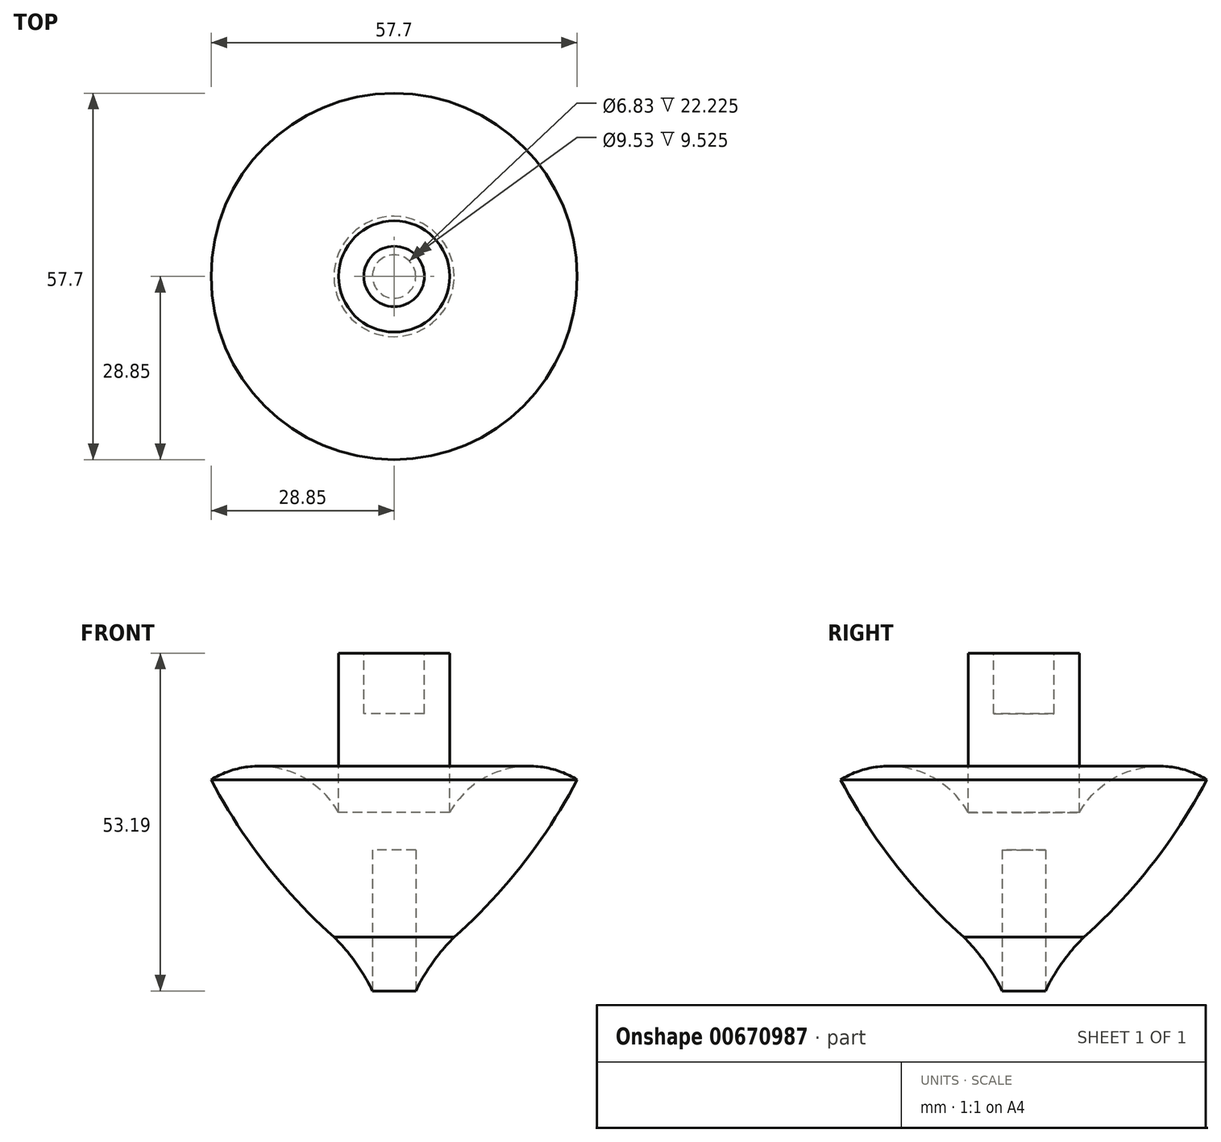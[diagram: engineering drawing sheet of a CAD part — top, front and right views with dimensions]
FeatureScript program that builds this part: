
annotation { "Feature Type Name" : "Feature", "Feature Type Description" : "" }
export const myFeature = defineFeature(function(context is Context, id is Id, definition is map)
    precondition{}
    {
        {
            var Q0;
            Q0=qCreatedBy(makeId("Front.planeOp"),FACE);
            var sketch = newSketch(context, id + "F0", { "sketchPlane" : qUnion([Q0])});
            skArc(sketch, "E0", {"start": v(9.48, 8.46) * mm, "mid": v(20.28, 20) * mm, "end": v(28.85, 33.28) * mm});
            skArc(sketch, "E1", {"start": v(28.85, 33.28) * mm, "mid": v(17.71, 34.95) * mm, "end": v(8.76, 28.11) * mm});
            skLineSegment(sketch, "E2", {"start": v(8.76, 28.11) * mm, "end": v(8.76, 53.19) * mm});
            skLineSegment(sketch, "E3", {"start": v(8.76, 53.19) * mm, "end": v(0, 53.19) * mm});
            skLineSegment(sketch, "E4", {"start": v(0, 53.19) * mm, "end": v(0, 0) * mm});
            skLineSegment(sketch, "E5", {"start": v(0, 0) * mm, "end": v(3.41, 0) * mm});
            skArc(sketch, "E6", {"start": v(9.48, 8.46) * mm, "mid": v(6.08, 4.5) * mm, "end": v(3.41, 0) * mm});
            skSolve(sketch);
        }
        {
            var Q0;
            Q0 = qSketchRegion(id + "F0", true);
            var Q1;
            Q1=sQuery(id+"F0.wireOp",EDGE,"E4");
            revolve(context, id + "F1", {"entities" : qUnion([Q0]), "axis" : qUnion([Q1]), "revolveType" : RevolveType.FULL, "surfaceOperationType" : NewSurfaceOperationType.NEW});
        }
        {
            var Q0;
            Q0=makeQuery(id+"F1.opRevolve","SWEPT_FACE",FACE,{"disambiguationData":[OSD([sQuery(id+"F0.wireOp",EDGE,"E3")])]});
            var sketch = newSketch(context, id + "F2", { "sketchPlane" : qUnion([Q0])});
            skCircle(sketch, "E7", {"center": v(0, 0) * mm, "radius": 4.76 * mm});
            skSolve(sketch);
        }
        {
            var Q0;
            Q0=makeQuery(id+"F1.opRevolve","SWEPT_FACE",FACE,{"disambiguationData":[OSD([sQuery(id+"F0.wireOp",EDGE,"E5")])]});
            extrude(context, id + "F3", {"entities" : qUnion([Q0]), "operationType" : NewBodyOperationType.REMOVE, "oppositeDirection" : true, "depth" : 22.22 * mm, "offsetDistance" : 25.4 * mm});
        }
        {
            var Q0;
            Q0 = qSketchRegion(id + "F2", true);
            extrude(context, id + "F4", {"entities" : qUnion([Q0]), "operationType" : NewBodyOperationType.REMOVE, "oppositeDirection" : true, "depth" : 9.52 * mm, "offsetDistance" : 25.4 * mm});
        }
    });
